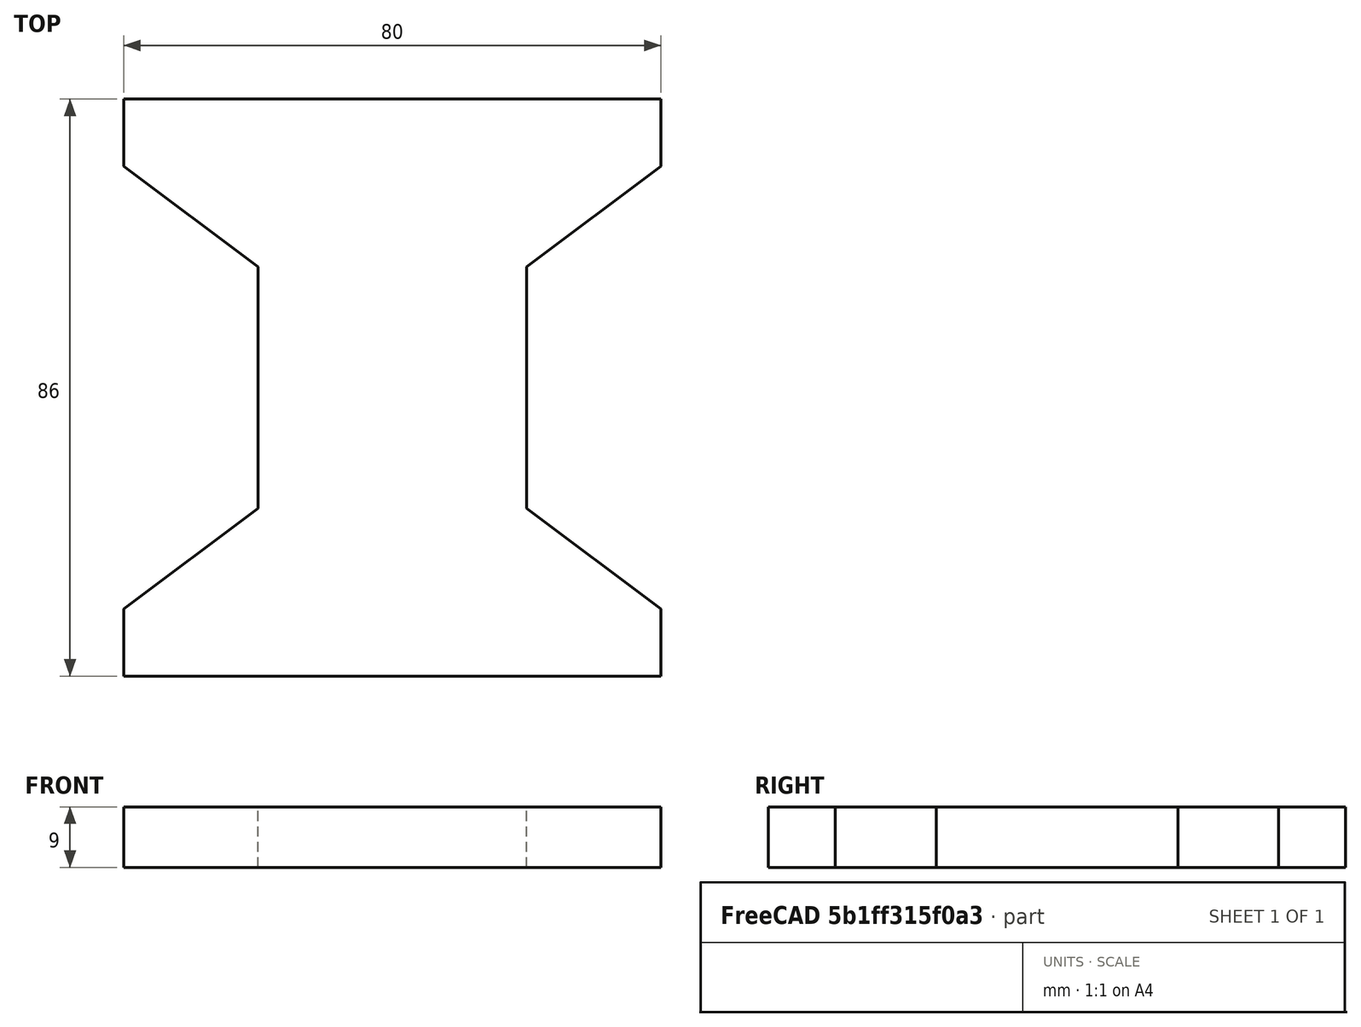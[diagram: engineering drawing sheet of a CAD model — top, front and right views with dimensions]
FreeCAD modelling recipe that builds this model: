
FCSTD DOCUMENT  (FreeCAD 0.16RUnknown)
Label: balise_gd
License: All rights reserved
LicenseURL: http://en.wikipedia.org/wiki/All_rights_reserved
objects: App::FeaturePython×7, Drawing::FeatureViewPart×4, App::DocumentObjectGroup×3, Drawing::FeatureViewPython×3, Part::Feature×2, Part::Plane×1, Part::Fuse×1, Part::Cut×1, Part::FeaturePython×1, Part::Extrusion×1, Drawing::FeaturePage×1
note: 7 computed .brp shape members not serialized (recipe doc carries the construction recipe); baked Part::Feature solids carry a one-line shape summary decoded from their .brp

FEATURE [Part::Plane] square
  Length = 80
  Width = 86
FEATURE [Part::Feature] polygon
  shape: bbox 20 x 66 x 2e-07 mm, 1 faces, 0 solids (baked)
FEATURE [Part::Feature] polygon001
  Placement = pos=(80,0,0) rot=(0,1,0;3.14159rad)
  shape: bbox 20 x 66 x 2e-07 mm, 1 faces, 0 solids (baked)
FEATURE [Part::Fuse] union
  Base = -> polygon
  Tool = -> polygon001
FEATURE [Part::Cut] difference
  Base = -> square
  Tool = -> union
FEATURE [Part::FeaturePython] RefineLinearExtrude  # WARN: FeaturePython — macro-defined, semantics opaque (R4)
  Base = -> difference
FEATURE [Part::Extrusion] LinearExtrude
  Base = -> RefineLinearExtrude
  Dir = (0,0,9)
  Solid = true
FEATURE [Drawing::FeatureViewPart] Ortho  label="Ortho_0_0"
  Direction = (1,0,0)
  HiddenWidth = 0.15
  LineWidth = 0.35
  Rotation = -90
  Scale = 1.5
  ShowHiddenLines = false
  ShowSmoothLines = false
  Source = -> LinearExtrude
  Tolerance = 0.05
  ViewResult = <g id="Ortho_0_0"\n   transform="rotate(-90,70.33,51.3333) translate(70.33,51.3333) scale(1.5,1.5)"\n  >\n<g   stroke="rgb(0, 0, 0)"\n   stroke-width="0.233333"\n   stroke-linecap="butt"\n   stroke-linejoin="miter"\n   fill="none"\n   transform="scale(1,-1)"\n  >\n<path id= "1" d=" M 0 -86 L 9 -86 " />\n<path id= "2" d=" M 0 -76 L 9 -76 " />\n<path id= "3" d=" M 0 -76 L 0 -86 " />\n<path id= "4" d=" M 9 -76 L 9 -86 " />\n<path id= "5" d=" M -2.44929e-15 -61 L 9 -61 " />\n<path id= "6" d=" M -2.44929e-15 -61 L 0 -76 " />\n<path id= "7" d=" M 9 -61 L 9 -76 " />\n<path id= "8" d=" M -2.44929e-15 -25 L 9 -25 " />\n<path id= "9" d=" M -2.44929e-15 -25 L -2.44929e-15 -61 " />\n<path id= "10" d=" M 9 -25 L 9 -61 " />\n<path id= "11" d=" M 0 -10 L 9 -10 " />\n<path id= "12" d=" M 0 -10 L -2.44929e-15 -25 " />\n<path id= "13" d=" M 9 -10 L 9 -25 " />\n<path id= "14" d=" M 0 0 L 9 0 " />\n<path id= "15" d=" M 0 0 L 0 -10 " />\n<path id= "16" d=" M 9 0 L 9 -10 " />\n</g>\n</g>
  Visible = true
  X = 70.33
  Y = 51.3333
FEATURE [Drawing::FeatureViewPart] Ortho001  label="Ortho_1_-1"
  Direction = (0.57735,-0.57735,0.57735)
  HiddenWidth = 0.15
  LineWidth = 0.35
  Rotation = 60
  Scale = 1.5
  ShowHiddenLines = false
  ShowSmoothLines = false
  Source = -> LinearExtrude
  Tolerance = 0.05
  ViewResult = <g id="Ortho_1_-1"\n   transform="rotate(60,221.63,146.515) translate(221.63,146.515) scale(1.5,1.5)"\n  >\n<g   stroke="rgb(0, 0, 0)"\n   stroke-width="0.233333"\n   stroke-linecap="butt"\n   stroke-linejoin="miter"\n   fill="none"\n   transform="scale(1,-1)"\n  >\n<path id= "1" d=" M 0 0 L -6.36396 3.67423 " />\n<path id= "2" d=" M -6.36396 3.67423 L -6.36396 11.8392 " />\n<path id= "3" d=" M -6.36396 11.8392 L 7.77817 32.2516 " />\n<path id= "4" d=" M 7.77817 32.2516 L 7.77817 61.6455 " />\n<path id= "5" d=" M 0 62.0537 L -6.36396 65.728 " />\n<path id= "6" d=" M 7.77817 59.8084 L -3.55271e-15 62.0537 " />\n<path id= "7" d=" M 7.77817 61.6455 L -6.36396 65.728 " />\n<path id= "8" d=" M -6.36396 65.728 L -6.36396 73.8929 " />\n<path id= "9" d=" M 56.5685 102.879 L 50.2046 106.553 " />\n<path id= "10" d=" M -6.36396 73.8929 L 50.2046 106.553 " />\n<path id= "11" d=" M 56.5685 94.7136 L 50.2046 98.3878 " />\n<path id= "12" d=" M 56.5685 94.7136 L 56.5685 102.879 " />\n<path id= "13" d=" M 50.2046 98.3878 L 50.2046 106.553 " />\n<path id= "14" d=" M 42.4264 74.3012 L 36.0624 77.9754 " />\n<path id= "15" d=" M 42.4264 74.3012 L 56.5685 94.7136 " />\n<path id= "16" d=" M 36.0624 77.9754 L 50.2046 98.3878 " />\n<path id= "17" d=" M 42.4264 46.7444 L 42.4264 74.3012 " />\n<path id= "18" d=" M 36.0624 48.5815 L 36.0624 77.9754 " />\n<path id= "19" d=" M 56.5685 40.8248 L 50.2046 44.4991 " />\n<path id= "20" d=" M 50.2046 44.4991 L 36.0624 48.5815 " />\n<path id= "21" d=" M 56.5685 32.6599 L 50.2046 36.3341 " />\n<path id= "22" d=" M 56.5685 32.6599 L 56.5685 40.8248 " />\n<path id= "23" d=" M 50.2046 36.3341 L 50.2046 44.4991 " />\n<path id= "24" d=" M 0 0 L 56.5685 32.6599 " />\n<path id= "25" d=" M -6.36396 3.67423 L 50.2046 36.3341 " />\n</g>\n</g>
  Visible = true
  X = 221.63
  Y = 146.515
FEATURE [Drawing::FeatureViewPart] Ortho004  label="Ortho_0_-1"
  Direction = (0,0,1)
  HiddenWidth = 0.15
  LineWidth = 0.35
  Rotation = 90
  Scale = 1.5
  ShowHiddenLines = false
  ShowSmoothLines = false
  Source = -> LinearExtrude
  Tolerance = 0.05
  ViewResult = <g id="Ortho_0_-1"\n   transform="rotate(90,70.33,79.1667) translate(70.33,79.1667) scale(1.5,1.5)"\n  >\n<g   stroke="rgb(0, 0, 0)"\n   stroke-width="0.233333"\n   stroke-linecap="butt"\n   stroke-linejoin="miter"\n   fill="none"\n   transform="scale(1,-1)"\n  >\n<path id= "1" d=" M 0 0 L 0 10 " />\n<path id= "2" d=" M 0 10 L 20 25 " />\n<path id= "3" d=" M 20 25 L 20 61 " />\n<path id= "4" d=" M 20 61 L 0 76 " />\n<path id= "5" d=" M 0 76 L 0 86 " />\n<path id= "6" d=" M 0 86 L 80 86 " />\n<path id= "7" d=" M 80 76 L 80 86 " />\n<path id= "8" d=" M 60 61 L 80 76 " />\n<path id= "9" d=" M 60 25 L 60 61 " />\n<path id= "10" d=" M 80 10 L 60 25 " />\n<path id= "11" d=" M 80 0 L 80 10 " />\n<path id= "12" d=" M 0 0 L 80 0 " />\n</g>\n</g>
  Visible = true
  X = 70.33
  Y = 79.1667
FEATURE [App::FeaturePython] Dimension011  # Draft dimension (typed FeaturePython)
  Dimline = (-6,0,0)
  Direction = (0,0,0)
  Distance = 86
  End = (0,0,0)
  Normal = (0,0,1)
  Start = (0,86,0)
FEATURE [App::FeaturePython] Dimension015  # Draft dimension (typed FeaturePython)
  Dimline = (0,0,15)
  Direction = (0,0,0)
  Distance = 10
  End = (0,86,9)
  Normal = (1,0,0)
  Start = (0,76,9)
FEATURE [App::FeaturePython] Dimension016  # Draft dimension (typed FeaturePython)
  Dimline = (0,0,15)
  Direction = (0,0,0)
  Distance = 15
  End = (0,76,9)
  Normal = (1,0,0)
  Start = (0,61,9)
FEATURE [App::FeaturePython] Dimension017  # Draft dimension (typed FeaturePython)
  Dimline = (0,0,15)
  Direction = (0,0,0)
  Distance = 36
  End = (0,61,9)
  Normal = (1,0,0)
  Start = (0,25,9)
FEATURE [App::DocumentObjectGroup] Groupe001  label="Dimensions YZ"
  Group = -> [Dimension015,Dimension016,Dimension017]
FEATURE [Drawing::FeatureViewPython] ViewGroupe001  label="Dimmensions YZ"  # drawing view (typed FeaturePython)
  Direction = (0,0,0)
  FillStyle = 0
  FontSize = 12
  LineStyle = 0
  LineWidth = 0.35
  Rotation = 90
  Scale = 1.5
  Source = -> Groupe001
  ViewResult = <blob: 2855 chars omitted>
  Visible = true
  X = 70.3
  Y = 46
FEATURE [Drawing::FeatureViewPart] View  label="Ortho_XZ"
  Direction = (0,1,0)
  HiddenWidth = 0.15
  LineWidth = 0.35
  Rotation = 0
  Scale = 1.5
  ShowHiddenLines = true
  ShowSmoothLines = false
  Source = -> LinearExtrude
  Tolerance = 0.05
  ViewResult = <g id="Ortho_XZ"\n   transform="rotate(0,26,199.15) translate(26,199.15) scale(1.5,1.5)"\n  >\n<g   stroke="rgb(0, 0, 0)"\n   stroke-width="0.1"\n   stroke-linecap="butt"\n   stroke-linejoin="miter"\n   stroke-dasharray="0.2,0.1"\n   fill="none"\n   transform="scale(1,-1)"\n  >\n<path id= "1" d=" M 0 0 L 9 0 " />\n<path id= "2" d=" M 0 0 L 9 0 " />\n<path id= "3" d=" M 0 20 L 9 20 " />\n<path id= "4" d=" M 0 0 L 0 20 " />\n<path id= "5" d=" M 9 0 L 9 20 " />\n<path id= "6" d=" M 0 20 L 9 20 " />\n<path id= "7" d=" M 0 0 L 9 0 " />\n<path id= "8" d=" M 0 20 L 0 0 " />\n<path id= "9" d=" M 9 20 L 9 0 " />\n<path id= "10" d=" M 0 80 L 9 80 " />\n<path id= "11" d=" M -2.44929e-15 60 L 9 60 " />\n<path id= "12" d=" M -2.44929e-15 60 L 0 80 " />\n<path id= "13" d=" M 9 60 L 9 80 " />\n<path id= "14" d=" M -2.44929e-15 60 L 9 60 " />\n<path id= "15" d=" M 9 80 L 9 60 " />\n<path id= "16" d=" M 0 80 L 9 80 " />\n<path id= "17" d=" M 0 0 L 0 80 " />\n<path id= "18" d=" M 9 0 L 9 80 " />\n</g>\n<g   stroke="rgb(0, 0, 0)"\n   stroke-width="0.233333"\n   stroke-linecap="butt"\n   stroke-linejoin="miter"\n   fill="none"\n   transform="scale(1,-1)"\n  >\n<path id= "1" d=" M 0 0 L 9 0 " />\n<path id= "2" d=" M 0 80 L 9 80 " />\n<path id= "3" d=" M 0 0 L 0 80 " />\n<path id= "4" d=" M 9 0 L 9 80 " />\n<path id= "5" d=" M 0 80 L 9 80 " />\n<path id= "6" d=" M 0 80 L -2.44929e-15 60 " />\n</g>\n</g>
  Visible = true
  X = 26
  Y = 199.15
FEATURE [App::FeaturePython] Dimension018  # Draft dimension (typed FeaturePython)
  Dimline = (0,0,15)
  Direction = (0,0,0)
  Distance = 20
  End = (80,0,9)
  Normal = (0,-1,0)
  Start = (60,0,9)
FEATURE [App::FeaturePython] Dimension019  # Draft dimension (typed FeaturePython)
  Dimline = (0,0,15)
  Direction = (0,0,0)
  Distance = 40
  End = (60,0,9)
  Normal = (0,-1,0)
  Start = (20,0,9)
FEATURE [App::DocumentObjectGroup] Groupe002  label="Dimensions XZ"
  Group = -> [Dimension018,Dimension019]
FEATURE [Drawing::FeatureViewPython] ViewGroupe002  label="Dimmensions XZ"  # drawing view (typed FeaturePython)
  Direction = (0,0,0)
  FillStyle = 0
  FontSize = 12
  LineStyle = 0
  LineWidth = 0.35
  Rotation = 90
  Scale = 1.5
  Source = -> Groupe002
  ViewResult = <g id="ViewGroupe002" transform="rotate(90.0,31.0,79.15) translate(31.0,79.15) scale(1.5,-1.5)"><path d="M 60.0 0.0 L 60.0 0.0 L 80.0 0.0 L 80.0 0.0" fill="none" stroke="#000000" stroke-width="0.233333333333 px" style="stroke-width:0.233333333333;stroke-miterlimit:4;stroke-dasharray:none" freecad:basepoint1="60.0 0.0" freecad:basepoint2="80.0 0.0" freecad:dimpoint="60.0 0.0"/>\n<path transform="rotate(-0.0,60.0,0.0) translate(60.0,0.0) scale(0.666666666667,0.666666666667)" freecad:skip="1" fill="#000000" stroke="none" style="stroke-miterlimit:4;stroke-dasharray:none" d="M 0 0 L 4 1 L 4 -1 Z"/>\n<path transform="rotate(180.0,80.0,0.0) translate(80.0,0.0) scale(0.666666666667,0.666666666667)" freecad:skip="1" fill="#000000" stroke="none" style="stroke-miterlimit:4;stroke-dasharray:none" d="M 0 0 L 4 1 L 4 -1 Z"/>\n<text fill="#000000" font-size="4.0" style="text-anchor:middle;text-align:center;font-family:" transform="rotate(-0.0,70.0,0.0) translate(70.0,0.0) scale(1,-1) " freecad:skip="1">\n20,00 </text>\n<path d="M 20.0 0.0 L 20.0 0.0 L 60.0 0.0 L 60.0 0.0" fill="none" stroke="#000000" stroke-width="0.233333333333 px" style="stroke-width:0.233333333333;stroke-miterlimit:4;stroke-dasharray:none" freecad:basepoint1="20.0 0.0" freecad:basepoint2="60.0 0.0" freecad:dimpoint="20.0 0.0"/>\n<path transform="rotate(-0.0,20.0,0.0) translate(20.0,0.0) scale(0.666666666667,0.666666666667)" freecad:skip="1" fill="#000000" stroke="none" style="stroke-miterlimit:4;stroke-dasharray:none" d="M 0 0 L 4 1 L 4 -1 Z"/>\n<path transform="rotate(180.0,60.0,0.0) translate(60.0,0.0) scale(0.666666666667,0.666666666667)" freecad:skip="1" fill="#000000" stroke="none" style="stroke-miterlimit:4;stroke-dasharray:none" d="M 0 0 L 4 1 L 4 -1 Z"/>\n<text fill="#000000" font-size="4.0" style="text-anchor:middle;text-align:center;font-family:" transform="rotate(-0.0,40.0,0.0) translate(40.0,0.0) scale(1,-1) " freecad:skip="1">\n40,00 </text>\n</g>
  Visible = true
  X = 31
  Y = 79.15
FEATURE [App::FeaturePython] Dimension  # Draft dimension (typed FeaturePython)
  Dimline = (0,-6,0)
  Direction = (0,0,0)
  Distance = 80
  End = (0,0,0)
  Normal = (0,0,1)
  Start = (80,0,0)
FEATURE [App::DocumentObjectGroup] Groupe  label="Dimensions XY"
  Group = -> [Dimension011,Dimension]
FEATURE [Drawing::FeatureViewPython] ViewGroupe  label="Dimmensions XY"  # drawing view (typed FeaturePython)
  Direction = (0,0,0)
  FillStyle = 0
  FontSize = 12
  LineStyle = 0
  LineWidth = 0.35
  Rotation = -90
  Scale = 1.5
  Source = -> Groupe
  ViewResult = <g id="ViewGroupe" transform="rotate(-90.0,199.3,199.15) translate(199.3,199.15) scale(1.5,-1.5)"><path d="M 0.0 86.0 L -6.0 86.0 L -6.0 0.0 L 0.0 0.0" fill="none" stroke="#000000" stroke-width="0.233333333333 px" style="stroke-width:0.233333333333;stroke-miterlimit:4;stroke-dasharray:none" freecad:basepoint1="0.0 86.0" freecad:basepoint2="0.0 0.0" freecad:dimpoint="-6.0 86.0"/>\n<path transform="rotate(-90.0,-6.0,86.0) translate(-6.0,86.0) scale(0.666666666667,0.666666666667)" freecad:skip="1" fill="#000000" stroke="none" style="stroke-miterlimit:4;stroke-dasharray:none" d="M 0 0 L 4 1 L 4 -1 Z"/>\n<path transform="rotate(90.0,-6.0,0.0) translate(-6.0,0.0) scale(0.666666666667,0.666666666667)" freecad:skip="1" fill="#000000" stroke="none" style="stroke-miterlimit:4;stroke-dasharray:none" d="M 0 0 L 4 1 L 4 -1 Z"/>\n<text fill="#000000" font-size="4.0" style="text-anchor:middle;text-align:center;font-family:" transform="rotate(-90.0,-5.0,43.0) translate(-5.0,43.0) scale(1,-1) " freecad:skip="1">\n86,00 </text>\n<path d="M 80.0 0.0 L 80.0 -6.0 L 0.0 -6.0 L 0.0 0.0" fill="none" stroke="#000000" stroke-width="0.233333333333 px" style="stroke-width:0.233333333333;stroke-miterlimit:4;stroke-dasharray:none" freecad:basepoint1="80.0 0.0" freecad:basepoint2="0.0 0.0" freecad:dimpoint="80.0 -6.0"/>\n<path transform="rotate(-180.0,80.0,-6.0) translate(80.0,-6.0) scale(0.666666666667,0.666666666667)" freecad:skip="1" fill="#000000" stroke="none" style="stroke-miterlimit:4;stroke-dasharray:none" d="M 0 0 L 4 1 L 4 -1 Z"/>\n<path transform="rotate(0.0,0.0,-6.0) translate(0.0,-6.0) scale(0.666666666667,0.666666666667)" freecad:skip="1" fill="#000000" stroke="none" style="stroke-miterlimit:4;stroke-dasharray:none" d="M 0 0 L 4 1 L 4 -1 Z"/>\n<text fill="#000000" font-size="4.0" style="text-anchor:middle;text-align:center;font-family:" transform="rotate(-180.0,40.0,-7.0) translate(40.0,-7.0) scale(1,-1) " freecad:skip="1">\n80,00 </text>\n</g>
  Visible = true
  X = 199.3
  Y = 199.15
FEATURE [Drawing::FeaturePage] Page
  EditableTexts = AUTHOR NAME | CREATION DATE | SUPERVISOR NAME | CHECK DATE | 1,5 | WEIGHT | NUMBER | SHEET | Balise | Plaque Gauche/Droite
  Group = -> [Ortho,Ortho001,Ortho004,ViewGroupe,ViewGroupe001,View,ViewGroupe002]
